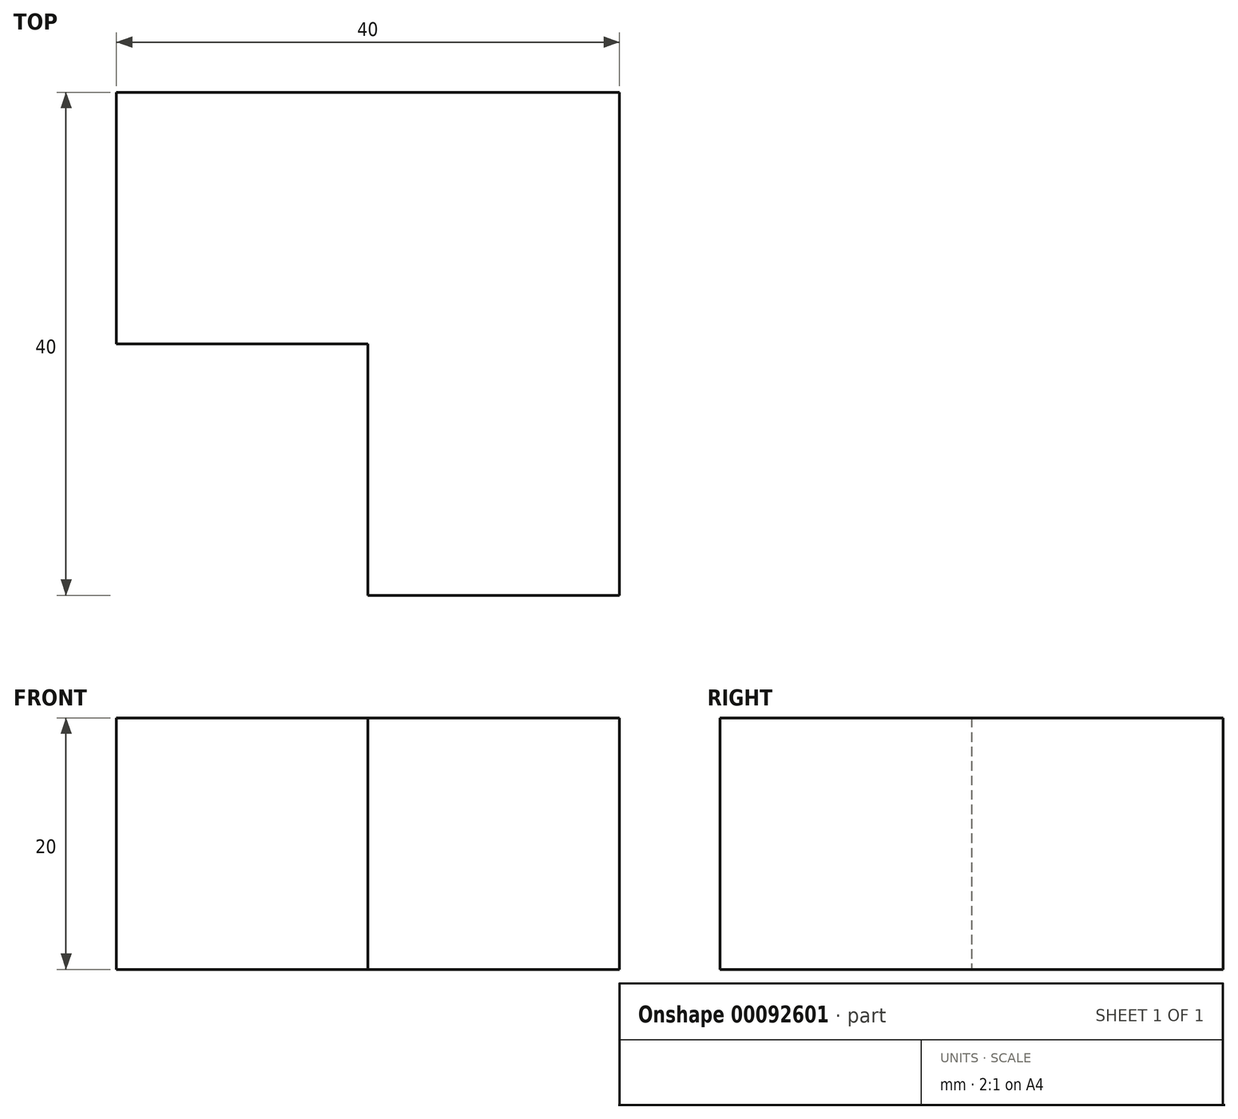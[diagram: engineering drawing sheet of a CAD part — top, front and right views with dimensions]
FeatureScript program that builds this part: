
annotation { "Feature Type Name" : "Feature", "Feature Type Description" : "" }
export const myFeature = defineFeature(function(context is Context, id is Id, definition is map)
    precondition{}
    {
        {
            var Q0;
            Q0=qCreatedBy(makeId("Top.planeOp"),FACE);
            var sketch = newSketch(context, id + "F0", { "sketchPlane" : qUnion([Q0])});
            skLineSegment(sketch, "E0.bottom", {"start": v(-25.5, 26) * mm, "end": v(14.5, 26) * mm});
            skLineSegment(sketch, "E0.top", {"start": v(-25.5, 6) * mm, "end": v(-5.5, 6) * mm});
            skLineSegment(sketch, "E0.left", {"start": v(-25.5, 26) * mm, "end": v(-25.5, 6) * mm});
            skLineSegment(sketch, "E0.right", {"start": v(14.5, 26) * mm, "end": v(14.5, 6) * mm});
            skLineSegment(sketch, "E1.top", {"start": v(-5.5, -14) * mm, "end": v(14.5, -14) * mm});
            skLineSegment(sketch, "E1.left", {"start": v(-5.5, 6) * mm, "end": v(-5.5, -14) * mm});
            skLineSegment(sketch, "E1.right", {"start": v(14.5, 6) * mm, "end": v(14.5, -14) * mm});
            skSolve(sketch);
        }
        {
            var Q0;
            Q0=makeQuery(id+"F0.imprint","IMPRINT",FACE,{"disambiguationData":[TD([[makeQuery(id+"F0.imprint","IMPRINT",EDGE,{"derivedFrom":sQuery(id+"F0.wireOp",EDGE,"E0.bottom")}),-1.0]])]});
            extrude(context, id + "F1", {"entities" : qUnion([Q0]), "depth" : 20 * mm});
        }
    });
